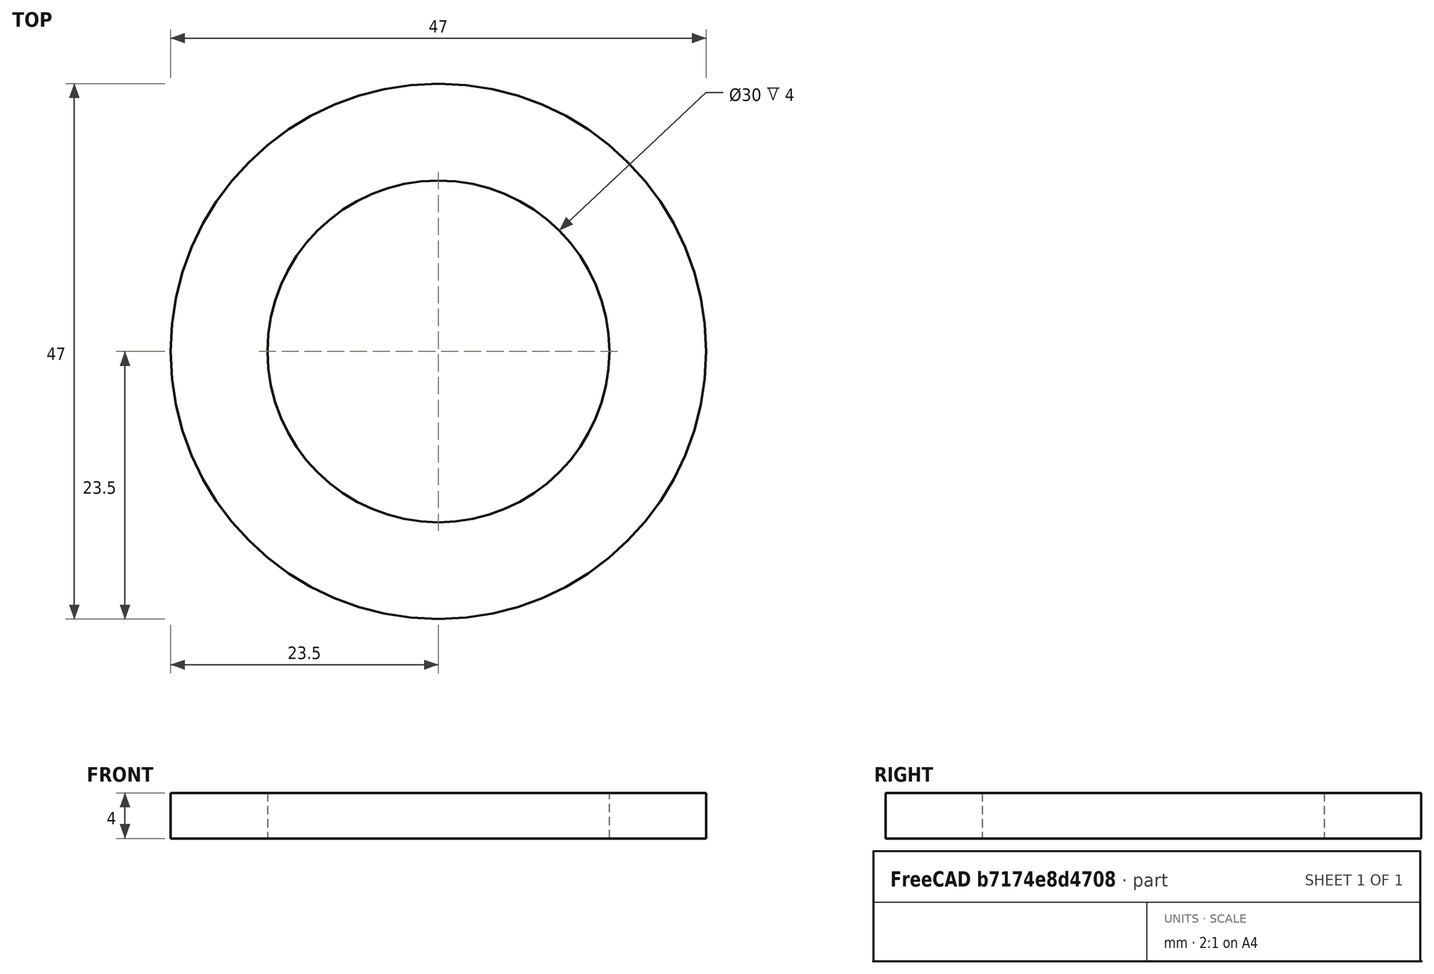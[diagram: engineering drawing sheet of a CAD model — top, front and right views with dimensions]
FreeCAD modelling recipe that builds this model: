
FCSTD DOCUMENT  (FreeCAD 0.19R24276 (Git))
Label: THRUST-30-47
License: All rights reserved
LicenseURL: http://en.wikipedia.org/wiki/All_rights_reserved
objects: Sketcher::SketchObject×1, PartDesign::Pad×1, PartDesign::Body×1, PartDesign::CoordinateSystem×1, App::Part×1
note: 5 computed .brp shape members not serialized (recipe doc carries the construction recipe); baked Part::Feature solids carry a one-line shape summary decoded from their .brp

FEATURE [Sketcher::SketchObject] Sketch
  FullyConstrained = false
  MapMode = 5
  Support = -> [XY_Plane]
  sketch-geometry (2):
    g0: Circle CenterX=0 CenterY=0 CenterZ=0 NormalX=0 NormalY=0 NormalZ=1 AngleXU=0 Radius=15
    g1: Circle CenterX=0 CenterY=0 CenterZ=0 NormalX=0 NormalY=0 NormalZ=1 AngleXU=0 Radius=23.5
  constraints (4):
    c: Coincident(g0,g-1)
    c: Coincident(g1,g0)
    c: Diameter(g1) = 47
    c: Diameter(g0) = 30
FEATURE [PartDesign::Pad] Pad
  AllowMultiFace = false
  Direction = (1,1,1)
  Length = 4
  Length2 = 100
  Profile = -> Sketch
  Type = 0
FEATURE [PartDesign::Body] Body
  Group = -> [Sketch,Pad]
  Origin = -> Origin
  Tip = -> Pad
FEATURE [PartDesign::CoordinateSystem] LCS_0
  AttacherType = Attacher::AttachEngine3D
  MapMode = 2
  Support = -> [X_Axis001]
FEATURE [App::Part] THRUST_30_47
  Group = -> [LCS_0,Body]
  Origin = -> Origin001
